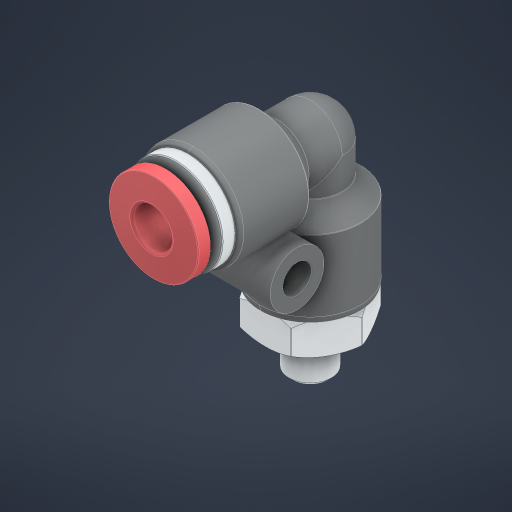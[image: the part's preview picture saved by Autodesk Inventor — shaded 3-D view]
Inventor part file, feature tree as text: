
AUTODESK INVENTOR PART (.ipt)
format: ipt  version: 2024 (Build 280153000, 153)  size: 565,760 bytes
history: native  units: in
note: dims shown in document units (in); Inventor stores cm internally (conversion verified against a paired STEP export)
features: other x4, revolve x1
ambient origin geometry x8: Origin, YZ Plane, XZ Plane, XY Plane, X Axis, Y Axis, Z Axis, Center Point
bodies: Solid1 (feature_tree), Solid2 (feature_tree), Solid3 (feature_tree), Solid4 (feature_tree), Solid5 (feature_tree)
feature tree (5):
  revolve  "Revolve3"  [1 undecoded]
  other  "Cut-Extrude1"
  other  "_276-8637-002 Rev1_-_Fillet2_"
  other  "_276-8637-002 Rev1_-_Fillet4_"
  parser-record x1  (decoder bookkeeping rows leaked as tree rows — omitted from the tree; the rows remain in map.json)
note: 1 required parameter value undecoded (feature->parameter linkage not recoverable at this tier; creation-order binding heuristic only, values carry confidence <= 0.55)
